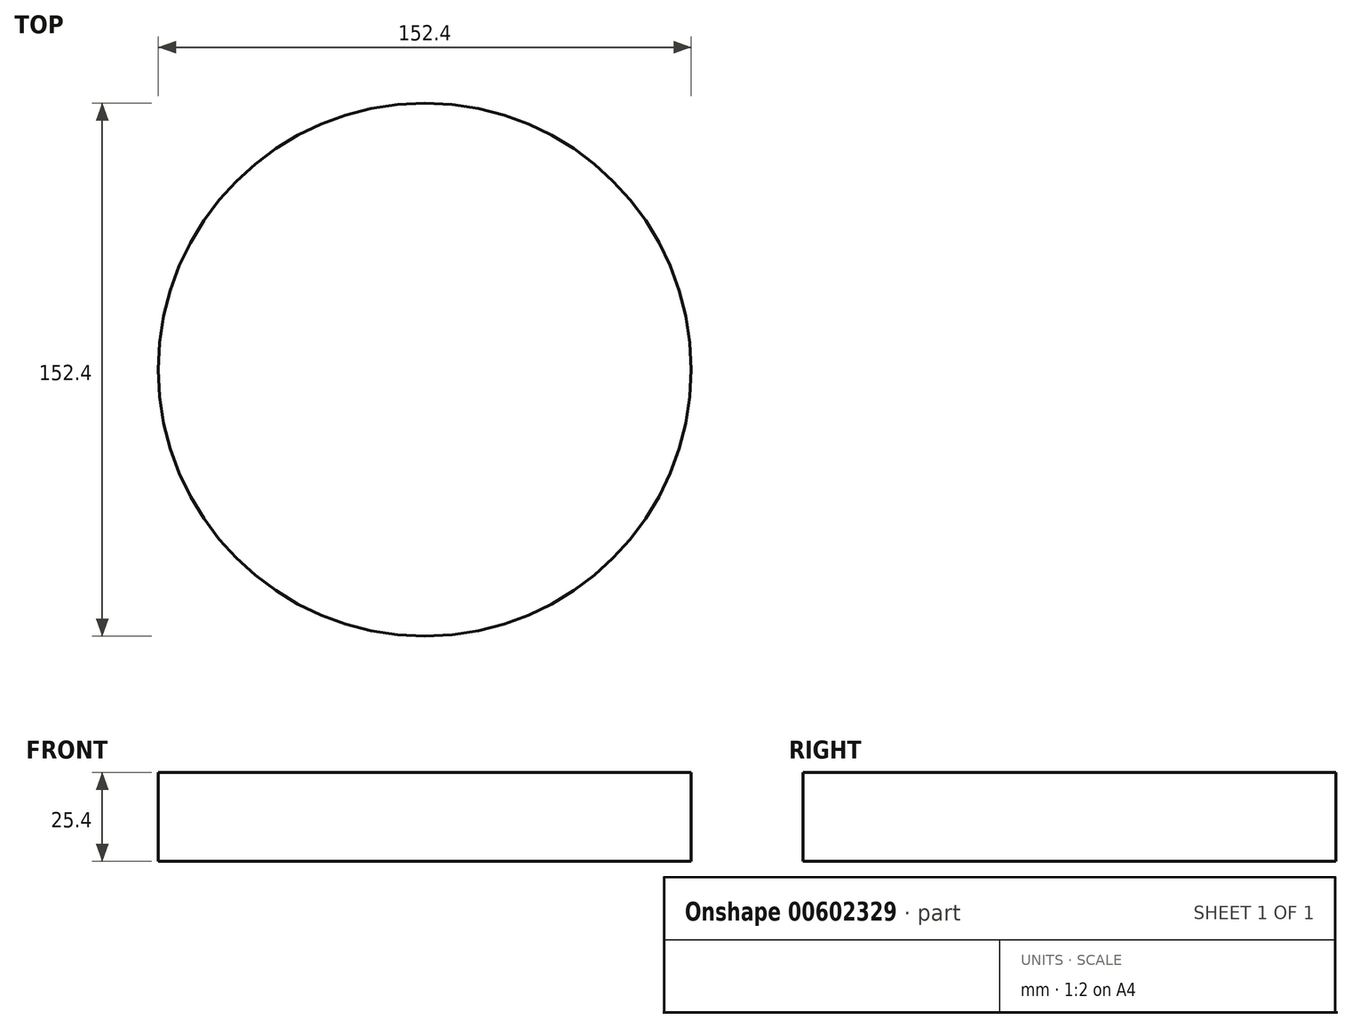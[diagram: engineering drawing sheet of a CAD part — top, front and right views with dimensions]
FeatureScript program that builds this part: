
annotation { "Feature Type Name" : "Feature", "Feature Type Description" : "" }
export const myFeature = defineFeature(function(context is Context, id is Id, definition is map)
    precondition{}
    {
        {
            var Q0;
            Q0=qCreatedBy(makeId("Top.planeOp"),FACE);
            var sketch = newSketch(context, id + "F0", { "sketchPlane" : qUnion([Q0])});
            skCircle(sketch, "E0", {"center": v(0, 0) * mm, "radius": 76.2 * mm});
            skSolve(sketch);
        }
        {
            var Q0;
            Q0=makeQuery(id+"F0.imprint","IMPRINT",FACE,{"disambiguationData":[TD([[makeQuery(id+"F0.imprint","IMPRINT",EDGE,{"derivedFrom":sQuery(id+"F0.wireOp",EDGE,"E0")}),1.0]])]});
            var Q1;
            Q1=sQuery(id+"F0.wireOp",EDGE,"E0");
            extrude(context, id + "F1", {"entities" : qUnion([Q0]), "surfaceEntities" : qUnion([Q1]), "depth" : 25.4 * mm, "offsetDistance" : 25.4 * mm});
        }
    });
